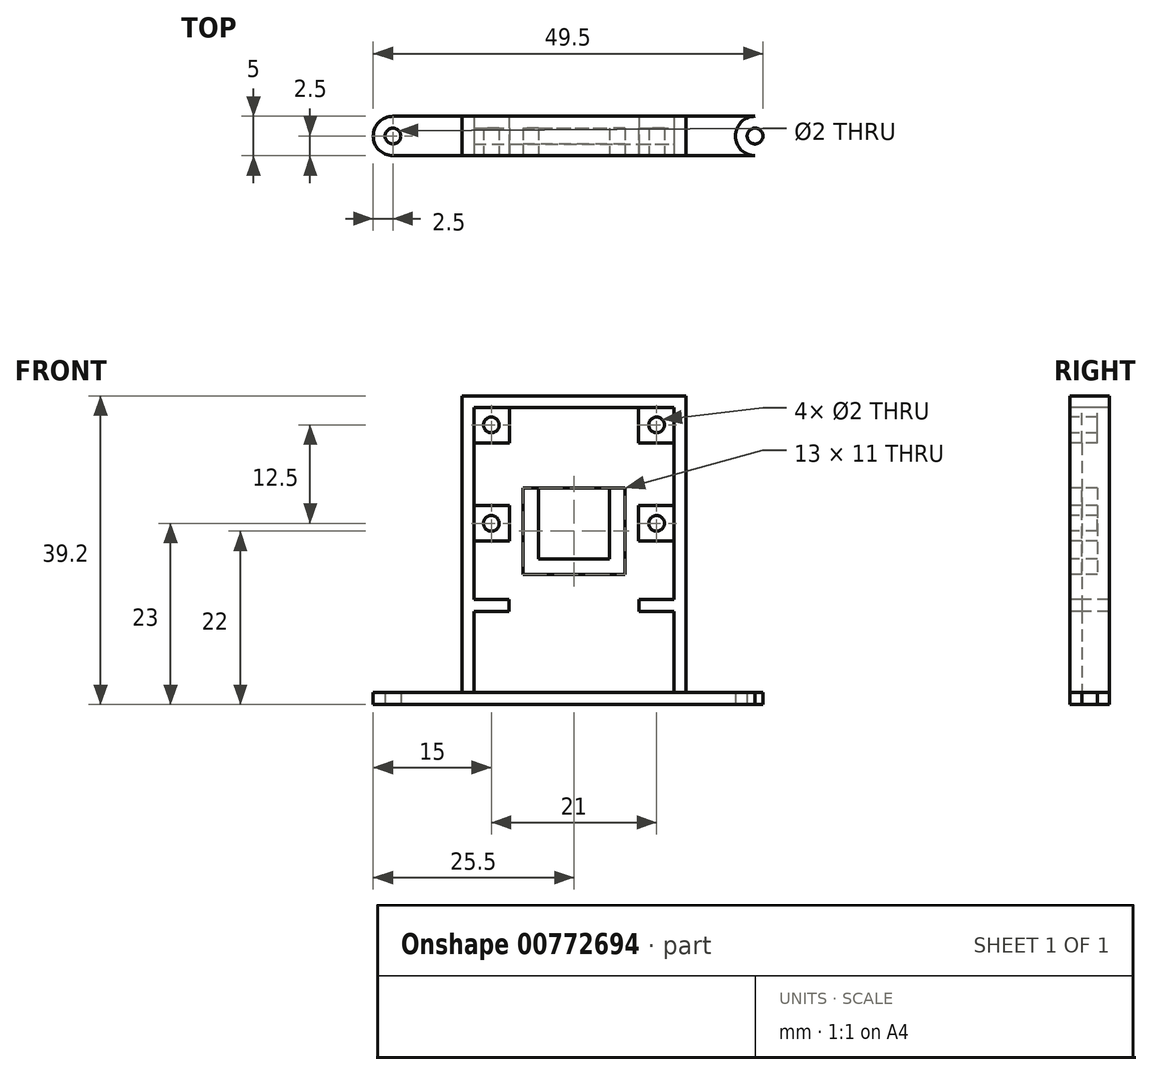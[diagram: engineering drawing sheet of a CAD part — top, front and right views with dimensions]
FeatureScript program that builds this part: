
annotation { "Feature Type Name" : "Feature", "Feature Type Description" : "" }
export const myFeature = defineFeature(function(context is Context, id is Id, definition is map)
    precondition{}
    {
        {
            var Q0;
            Q0=qCreatedBy(makeId("Top.planeOp"),FACE);
            var sketch = newSketch(context, id + "F0", { "sketchPlane" : qUnion([Q0])});
            skLineSegment(sketch, "E0.bottom", {"start": v(-23, 2.5) * mm, "end": v(23, 2.5) * mm});
            skLineSegment(sketch, "E0.top", {"start": v(-23, -2.5) * mm, "end": v(23, -2.5) * mm});
            skCircle(sketch, "E1", {"center": v(-23, 0) * mm, "radius": 2.5 * mm});
            skCircle(sketch, "E2.MirrorC", {"center": v(23, 0) * mm, "radius": 2.5 * mm});
            skCircle(sketch, "E3", {"center": v(-23, 0) * mm, "radius": 1 * mm});
            skCircle(sketch, "E4.MirrorC", {"center": v(23, 0) * mm, "radius": 1 * mm});
            skSolve(sketch);
        }
        {
            var Q0;
            Q0=makeQuery(id+"F0.imprint","IMPRINT",FACE,{"disambiguationData":[TD([[makeQuery(id+"F0.imprint","IMPRINT",EDGE,{"derivedFrom":sQuery(id+"F0.wireOp",EDGE,"E3")}),-1.0]])]});
            var Q1;
            {var subQ0=sQuery(id+"F0.wireOp",EDGE,"E0.bottom");Q1=makeQuery(id+"F0.imprint","IMPRINT",FACE,{"disambiguationData":[TD([[makeQuery(id+"F0.imprint","IMPRINT",EDGE,{"derivedFrom":subQ0}),-1.0]])]});}
            var Q2;
            Q2=makeQuery(id+"F0.imprint","IMPRINT",FACE,{"disambiguationData":[TD([[makeQuery(id+"F0.imprint","IMPRINT",EDGE,{"derivedFrom":sQuery(id+"F0.wireOp",EDGE,"E4.MirrorC")}),1.0]])]});
            extrude(context, id + "F1", {"entities" : qUnion([Q0, Q1, Q2]), "depth" : 1.5 * mm, "offsetDistance" : 25 * mm});
        }
        {
            var Q0;
            Q0=makeQuery(id+"F1.opExtrude","SWEPT_FACE",FACE,{"disambiguationData":[OSD([sQuery(id+"F0.wireOp",EDGE,"E0.top")])]});
            var sketch = newSketch(context, id + "F2", { "sketchPlane" : qUnion([Q0])});
            skLineSegment(sketch, "E5.bottom", {"start": v(-12.5, 37.5) * mm, "end": v(12.5, 37.5) * mm, "construction": true});
            skLineSegment(sketch, "E5.top", {"start": v(-12.5, 13.5) * mm, "end": v(12.5, 13.5) * mm, "construction": true});
            skLineSegment(sketch, "E5.left", {"start": v(-12.5, 37.5) * mm, "end": v(-12.5, 13.5) * mm, "construction": true});
            skLineSegment(sketch, "E5.right", {"start": v(12.5, 37.5) * mm, "end": v(12.5, 13.5) * mm, "construction": true});
            skLineSegment(sketch, "E6.bottom", {"start": v(-4.5, 27.5) * mm, "end": v(4.5, 27.5) * mm});
            skLineSegment(sketch, "E6.top", {"start": v(-4.5, 18.5) * mm, "end": v(4.5, 18.5) * mm});
            skLineSegment(sketch, "E6.left", {"start": v(-4.5, 27.5) * mm, "end": v(-4.5, 18.5) * mm});
            skLineSegment(sketch, "E6.right", {"start": v(4.5, 27.5) * mm, "end": v(4.5, 18.5) * mm});
            skLineSegment(sketch, "E7", {"start": v(-16.59, 23) * mm, "end": v(16.18, 23) * mm, "construction": true});
            skCircle(sketch, "E8", {"center": v(10.5, 23) * mm, "radius": 1 * mm});
            skCircle(sketch, "E9", {"center": v(-10.5, 23) * mm, "radius": 1 * mm});
            skCircle(sketch, "E10", {"center": v(-10.5, 35.5) * mm, "radius": 1 * mm});
            skCircle(sketch, "E11", {"center": v(10.5, 35.5) * mm, "radius": 1 * mm});
            skLineSegment(sketch, "E12", {"start": v(-4.5, 27.5) * mm, "end": v(-6.5, 27.5) * mm});
            skLineSegment(sketch, "E13", {"start": v(-6.5, 27.5) * mm, "end": v(-6.5, 16.5) * mm});
            skLineSegment(sketch, "E14", {"start": v(-6.5, 16.5) * mm, "end": v(6.5, 16.5) * mm});
            skLineSegment(sketch, "E15", {"start": v(6.5, 16.5) * mm, "end": v(6.5, 27.5) * mm});
            skLineSegment(sketch, "E16", {"start": v(6.5, 27.5) * mm, "end": v(4.5, 27.5) * mm});
            skLineSegment(sketch, "E17.bottom", {"start": v(-12.7, 37.7) * mm, "end": v(12.7, 37.7) * mm});
            skLineSegment(sketch, "E17.top", {"start": v(-12.7, 1.5) * mm, "end": v(12.7, 1.5) * mm});
            skLineSegment(sketch, "E17.left", {"start": v(-12.7, 37.7) * mm, "end": v(-12.7, 13.3) * mm});
            skLineSegment(sketch, "E17.right", {"start": v(12.7, 37.7) * mm, "end": v(12.7, 13.3) * mm});
            skLineSegment(sketch, "E18.bottom", {"start": v(-14.2, 39.2) * mm, "end": v(14.2, 39.2) * mm});
            skLineSegment(sketch, "E18.top", {"start": v(-14.2, 1.5) * mm, "end": v(14.2, 1.5) * mm});
            skLineSegment(sketch, "E18.left", {"start": v(-14.2, 39.2) * mm, "end": v(-14.2, 1.5) * mm});
            skLineSegment(sketch, "E18.right", {"start": v(14.2, 39.2) * mm, "end": v(14.2, 1.5) * mm});
            skLineSegment(sketch, "E19", {"start": v(-12.7, 13.3) * mm, "end": v(-8.25, 13.3) * mm});
            skLineSegment(sketch, "E20", {"start": v(-12.7, 11.8) * mm, "end": v(-8.25, 11.8) * mm});
            skLineSegment(sketch, "E21.trimOffspring", {"start": v(-12.7, 11.8) * mm, "end": v(-12.7, 1.5) * mm});
            skLineSegment(sketch, "E22.trimOffspring", {"start": v(12.7, 11.8) * mm, "end": v(12.7, 1.5) * mm});
            skLineSegment(sketch, "E23", {"start": v(-12.7, 33.2) * mm, "end": v(-8.2, 33.2) * mm});
            skLineSegment(sketch, "E24", {"start": v(-8.2, 33.2) * mm, "end": v(-8.2, 37.7) * mm});
            skLineSegment(sketch, "E25", {"start": v(-12.7, 25.25) * mm, "end": v(-8.2, 25.25) * mm});
            skLineSegment(sketch, "E26", {"start": v(-8.2, 25.25) * mm, "end": v(-8.2, 20.75) * mm});
            skLineSegment(sketch, "E27", {"start": v(-8.2, 20.75) * mm, "end": v(-12.7, 20.75) * mm});
            skLineSegment(sketch, "E28.MirrorCS", {"start": v(8.2, 33.2) * mm, "end": v(8.2, 37.7) * mm});
            skLineSegment(sketch, "E29.MirrorCS", {"start": v(12.7, 33.2) * mm, "end": v(8.2, 33.2) * mm});
            skLineSegment(sketch, "E30.MirrorCS", {"start": v(8.2, 20.75) * mm, "end": v(12.7, 20.75) * mm});
            skLineSegment(sketch, "E31.MirrorCS", {"start": v(12.7, 25.25) * mm, "end": v(8.2, 25.25) * mm});
            skLineSegment(sketch, "E32.MirrorCS", {"start": v(8.2, 25.25) * mm, "end": v(8.2, 20.75) * mm});
            skLineSegment(sketch, "E33", {"start": v(8.25, 13.3) * mm, "end": v(8.25, 11.8) * mm});
            skLineSegment(sketch, "E34", {"start": v(-8.25, 13.3) * mm, "end": v(-8.25, 11.8) * mm});
            skLineSegment(sketch, "E35.trimOffspring", {"start": v(8.25, 11.8) * mm, "end": v(12.7, 11.8) * mm});
            skLineSegment(sketch, "E36.trimOffspring", {"start": v(8.25, 13.3) * mm, "end": v(12.7, 13.3) * mm});
            skSolve(sketch);
        }
        {
            var Q0;
            Q0=makeQuery(id+"F2.imprint","IMPRINT",FACE,{"disambiguationData":[TD([[makeQuery(id+"F2.imprint","IMPRINT",EDGE,{"derivedFrom":sQuery(id+"F2.wireOp",EDGE,"E20")}),-1.0]])]});
            var Q1;
            Q1=makeQuery(id+"F2.imprint","IMPRINT",FACE,{"disambiguationData":[TD([[makeQuery(id+"F2.imprint","IMPRINT",EDGE,{"derivedFrom":sQuery(id+"F2.wireOp",EDGE,"E6.bottom")}),1.0]])]});
            extrude(context, id + "F3", {"entities" : qUnion([Q0, Q1]), "oppositeDirection" : true, "depth" : 1.5 * mm, "offsetDistance" : 25 * mm});
        }
        {
            var Q0;
            Q0=makeQuery(id+"F2.imprint","IMPRINT",FACE,{"disambiguationData":[TD([[makeQuery(id+"F2.imprint","IMPRINT",EDGE,{"derivedFrom":sQuery(id+"F2.wireOp",EDGE,"E18.bottom")}),-1.0]])]});
            extrude(context, id + "F4", {"entities" : qUnion([Q0]), "oppositeDirection" : true, "depth" : 5 * mm, "offsetDistance" : 25 * mm});
        }
        {
            var Q0;
            Q0=makeQuery(id+"F2.imprint","IMPRINT",FACE,{"disambiguationData":[TD([[makeQuery(id+"F2.imprint","IMPRINT",EDGE,{"derivedFrom":sQuery(id+"F2.wireOp",EDGE,"E11")}),-1.0]])]});
            var Q1;
            Q1=makeQuery(id+"F2.imprint","IMPRINT",FACE,{"disambiguationData":[TD([[makeQuery(id+"F2.imprint","IMPRINT",EDGE,{"derivedFrom":sQuery(id+"F2.wireOp",EDGE,"E8")}),-1.0]])]});
            var Q2;
            Q2=makeQuery(id+"F2.imprint","IMPRINT",FACE,{"disambiguationData":[TD([[makeQuery(id+"F2.imprint","IMPRINT",EDGE,{"derivedFrom":sQuery(id+"F2.wireOp",EDGE,"E6.top")}),-1.0]])]});
            var Q3;
            Q3=makeQuery(id+"F2.imprint","IMPRINT",FACE,{"disambiguationData":[TD([[makeQuery(id+"F2.imprint","IMPRINT",EDGE,{"derivedFrom":sQuery(id+"F2.wireOp",EDGE,"E10")}),-1.0]])]});
            var Q4;
            Q4=makeQuery(id+"F2.imprint","IMPRINT",FACE,{"disambiguationData":[TD([[makeQuery(id+"F2.imprint","IMPRINT",EDGE,{"derivedFrom":sQuery(id+"F2.wireOp",EDGE,"E9")}),-1.0]])]});
            extrude(context, id + "F5", {"entities" : qUnion([Q0, Q1, Q2, Q3, Q4]), "oppositeDirection" : true, "depth" : 3.5 * mm, "offsetDistance" : 25 * mm});
        }
    });
